# Revit family: Hand_Dryer-Excel-Dryer-Recess_Mounting_Kit
name_source: partatom
category: Specialty Equipment
revit_build: Autodesk Revit 2015 (Build: 20140606_1530(x64)
units: mm (PartAtom-declared; Revit-internal decimal feet)

## types (1)
- Recess Kit
    BIMobject category = Dryers (Hand & Hair)
    Body = Metal -  ExcelDryer -Stainless Stainless - #4 Satin Finish
    Date of publishing = 3/6/2017
    Default Elevation = 2' - 11 1/2"
    Depth = 0' - 3 3/8"
    Description = ADA Compliant Recess Kit
    Design country = United States
    Edition number = 1
    Frame Height = 2' - 2"
    Frame Width = 1' - 4 3/8"
    Height = 2' - 0 1/8"
    Manufacturer = Excel Dryer
    Manufacturer country = United States
    Manufacturer name = Excel Dryer US
    Material main = Zink
    Model = #40502 Recess Kit
    Nominal height = 0' - 0"
    Nominal width = 0' - 0"
    Product Documentation Link = http://www.exceldryer.com
    Product Guid = 0cda2fda-f62e-4f02-ad92-43a2561d0f9c
    Product Page URL = http://www.exceldryer.com
    Product SKU = excel_xlerator_ADA_compliance_recess_kit
    Product data url = https://bimobject.com
    Product family = Equipment
    Product group = Hand dryer
    Product url = http://www.exceldryer.com
    QR code = http://bimobject.com
    URL = http://www.exceldryer.com
    Weight Net (Kg) = 0
    Width = 1' - 2 3/8"

## geometry (parser evidence)
native form markers: Blend x4, Sweep x1
no freeform markers — native parametric forms only
